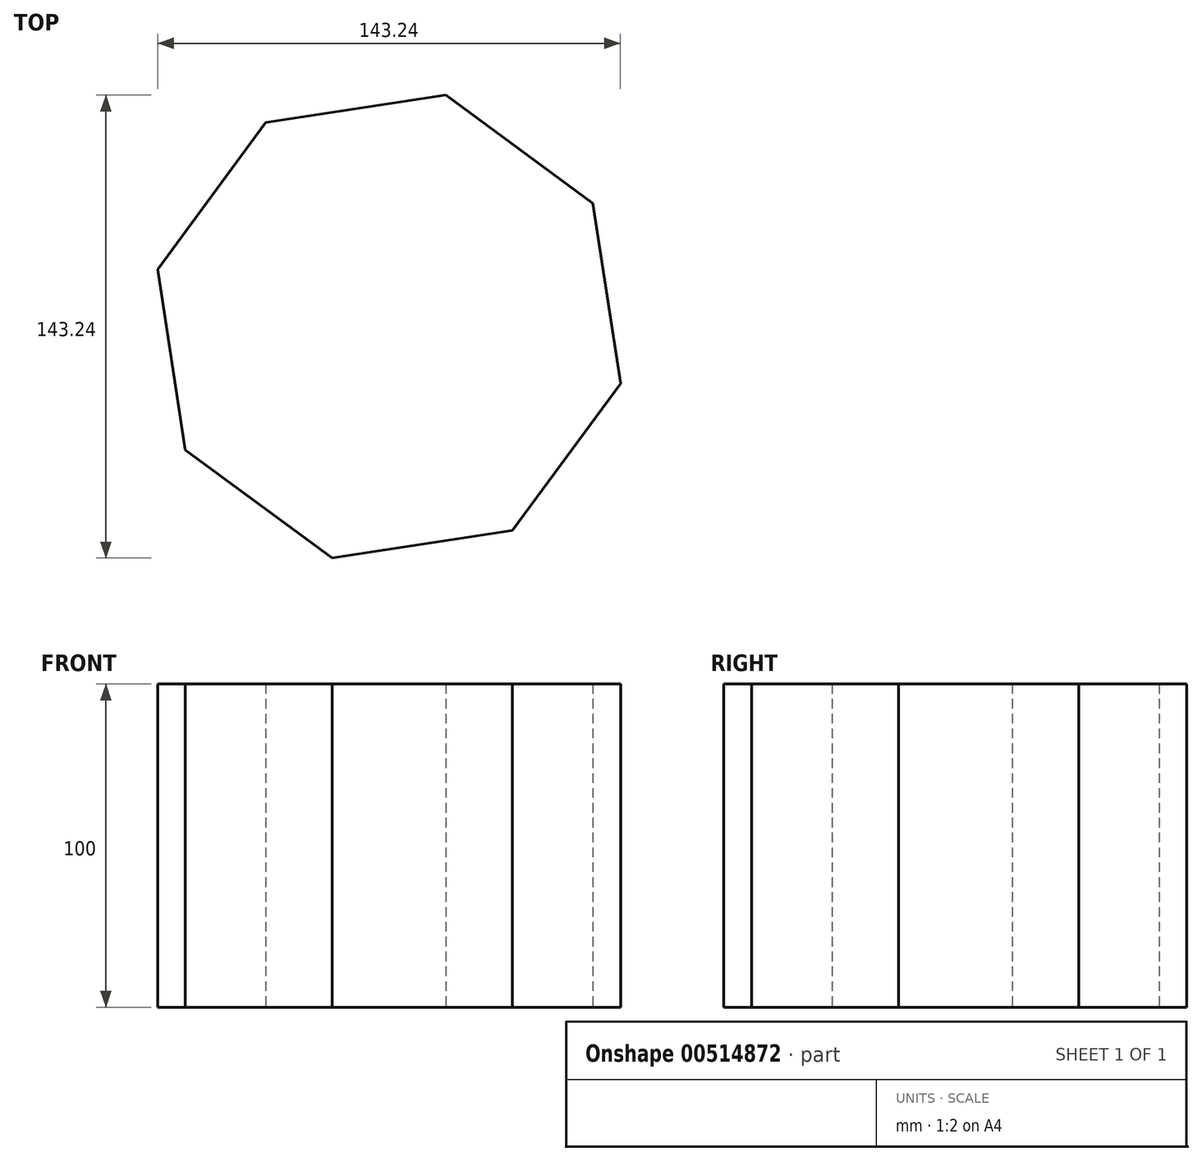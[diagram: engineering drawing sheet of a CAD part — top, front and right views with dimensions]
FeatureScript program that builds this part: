
annotation { "Feature Type Name" : "Feature", "Feature Type Description" : "" }
export const myFeature = defineFeature(function(context is Context, id is Id, definition is map)
    precondition{}
    {
        {
            var Q0;
            Q0=qCreatedBy(makeId("Top.planeOp"),FACE);
            var sketch = newSketch(context, id + "F0", { "sketchPlane" : qUnion([Q0])});
            skCircle(sketch, "E0.cCircle", {"center": v(0, 0) * mm, "radius": 73.76 * mm, "construction": true});
            skLineSegment(sketch, "E0.0", {"start": v(-38.18, 63.1) * mm, "end": v(17.62, 71.62) * mm});
            skLineSegment(sketch, "E0.1", {"start": v(17.62, 71.62) * mm, "end": v(63.1, 38.18) * mm});
            skLineSegment(sketch, "E0.2", {"start": v(63.1, 38.18) * mm, "end": v(71.62, -17.62) * mm});
            skLineSegment(sketch, "E0.3", {"start": v(71.62, -17.62) * mm, "end": v(38.18, -63.1) * mm});
            skLineSegment(sketch, "E0.4", {"start": v(38.18, -63.1) * mm, "end": v(-17.62, -71.62) * mm});
            skLineSegment(sketch, "E0.5", {"start": v(-17.62, -71.62) * mm, "end": v(-63.1, -38.18) * mm});
            skLineSegment(sketch, "E0.6", {"start": v(-63.1, -38.18) * mm, "end": v(-71.62, 17.62) * mm});
            skLineSegment(sketch, "E0.7", {"start": v(-71.62, 17.62) * mm, "end": v(-38.18, 63.1) * mm});
            skSolve(sketch);
        }
        {
            var Q0;
            Q0=makeQuery(id+"F0.imprint","IMPRINT",FACE,{"disambiguationData":[TD([[makeQuery(id+"F0.imprint","IMPRINT",EDGE,{"derivedFrom":sQuery(id+"F0.wireOp",EDGE,"E0.0")}),-1.0]])]});
            extrude(context, id + "F1", {"entities" : qUnion([Q0]), "depth" : 100 * mm, "offsetDistance" : 25.4 * mm});
        }
    });
